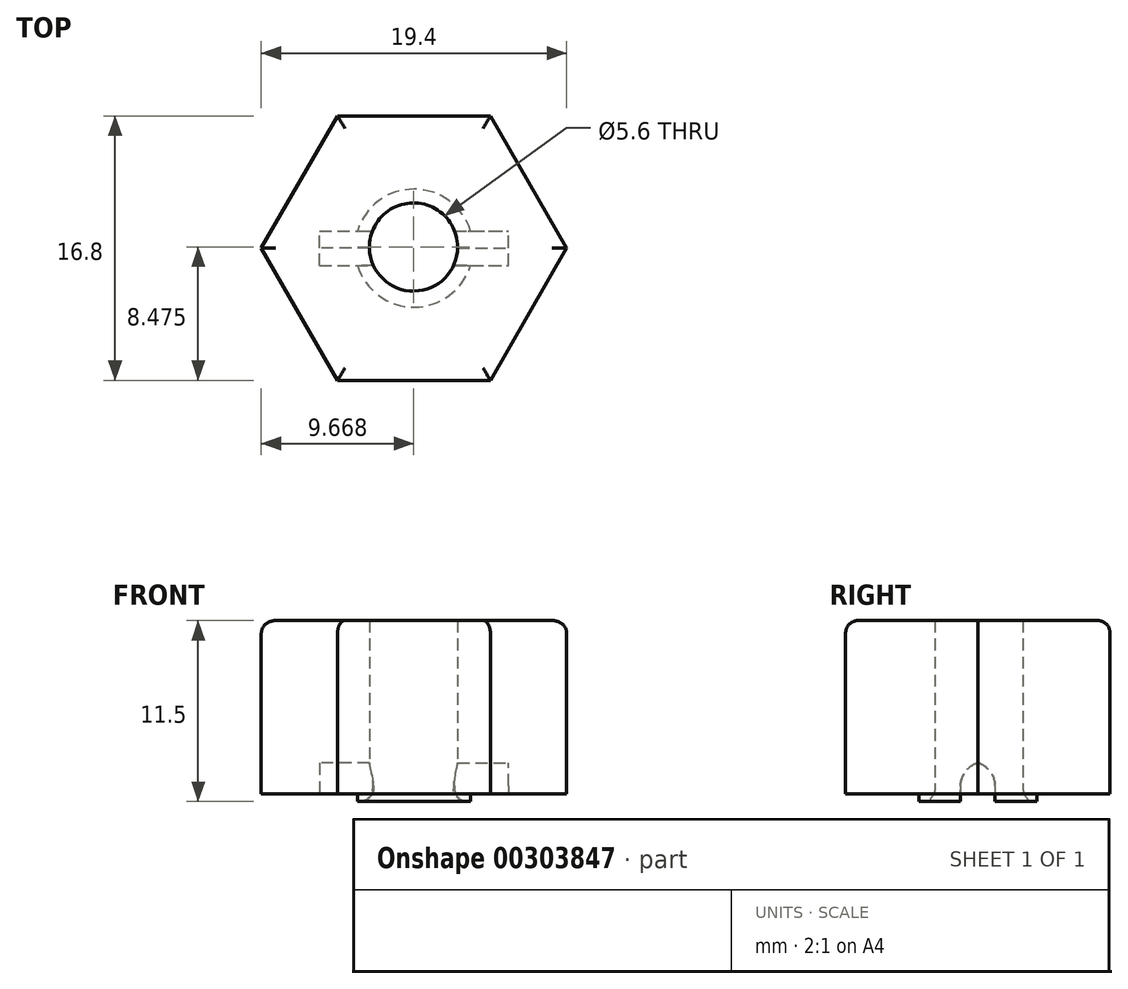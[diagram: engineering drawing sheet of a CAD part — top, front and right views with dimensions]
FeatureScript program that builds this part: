
annotation { "Feature Type Name" : "Feature", "Feature Type Description" : "" }
export const myFeature = defineFeature(function(context is Context, id is Id, definition is map)
    precondition{}
    {
        {
            var Q0;
            Q0=qCreatedBy(makeId("Top.planeOp"),FACE);
            var sketch = newSketch(context, id + "F0", { "sketchPlane" : qUnion([Q0])});
            skCircle(sketch, "E0.cCircle", {"center": v(0, 0) * mm, "radius": 8.4 * mm, "construction": true});
            skLineSegment(sketch, "E0.0", {"start": v(9.7, 0) * mm, "end": v(4.85, -8.4) * mm});
            skLineSegment(sketch, "E0.1", {"start": v(4.85, -8.4) * mm, "end": v(-4.85, -8.4) * mm});
            skLineSegment(sketch, "E0.2", {"start": v(-4.85, -8.4) * mm, "end": v(-9.7, 0) * mm});
            skLineSegment(sketch, "E0.3", {"start": v(-9.7, 0) * mm, "end": v(-4.85, 8.4) * mm});
            skLineSegment(sketch, "E0.4", {"start": v(-4.85, 8.4) * mm, "end": v(4.85, 8.4) * mm});
            skLineSegment(sketch, "E0.5", {"start": v(4.85, 8.4) * mm, "end": v(9.7, 0) * mm});
            skPoint(sketch, "E0.0.midPoint", {"position": v(7.27, -4.2) * mm});
            skCircle(sketch, "E1", {"center": v(-0.03, 0.07) * mm, "radius": 2.8 * mm});
            skSolve(sketch);
        }
        {
            var Q0;
            Q0=makeQuery(id+"F0.imprint","IMPRINT",FACE,{"disambiguationData":[TD([[makeQuery(id+"F0.imprint","IMPRINT",EDGE,{"derivedFrom":sQuery(id+"F0.wireOp",EDGE,"E0.0")}),-1.0]])]});
            extrude(context, id + "F1", {"entities" : qUnion([Q0]), "depth" : 11 * mm, "offsetDistance" : 25 * mm});
        }
        {
            var Q0;
            Q0=qCreatedBy(makeId("Top.planeOp"),FACE);
            var sketch = newSketch(context, id + "F2", { "sketchPlane" : qUnion([Q0])});
            skLineSegment(sketch, "E2.bottom", {"start": v(-6, -1.1) * mm, "end": v(6, -1.1) * mm});
            skLineSegment(sketch, "E2.top", {"start": v(-6, 1.1) * mm, "end": v(6, 1.1) * mm});
            skLineSegment(sketch, "E2.left", {"start": v(-6, -1.1) * mm, "end": v(-6, 1.1) * mm});
            skLineSegment(sketch, "E2.right", {"start": v(6, -1.1) * mm, "end": v(6, 1.1) * mm});
            skCircle(sketch, "E3", {"center": v(0, 0) * mm, "radius": 3.75 * mm});
            skSolve(sketch);
        }
        {
            var Q0;
            Q0=makeQuery(id+"F2.imprint","IMPRINT",FACE,{"disambiguationData":[TD([[makeQuery(id+"F2.imprint","IMPRINT",EDGE,{"derivedFrom":sQuery(id+"F2.wireOp",EDGE,"E2.bottom")}),1.0]])]});
            extrude(context, id + "F3", {"entities" : qUnion([Q0]), "operationType" : NewBodyOperationType.REMOVE, "depth" : 2 * mm, "offsetDistance" : 25 * mm});
        }
        {
            var Q0;
            Q0=makeQuery(id+"F1.opExtrude","CAP_FACE",FACE,{"disambiguationData":[OSD([sQuery(id+"F0.wireOp",EDGE,"E0.0"),sQuery(id+"F0.wireOp",EDGE,"E0.1"),sQuery(id+"F0.wireOp",EDGE,"E0.2"),sQuery(id+"F0.wireOp",EDGE,"E0.3"),sQuery(id+"F0.wireOp",EDGE,"E0.4"),sQuery(id+"F0.wireOp",EDGE,"E0.5"),sQuery(id+"F0.wireOp",EDGE,"E1")])],"isStart":true});
            var sketch = newSketch(context, id + "F4", { "sketchPlane" : qUnion([Q0])});
            skCircle(sketch, "E4", {"center": v(0, 0) * mm, "radius": 3.75 * mm});
            skSolve(sketch);
        }
        {
            var Q0;
            {var subQ1=sQuery(id+"F0.wireOp",EDGE,"E1");var subQ4=sQuery(id+"F2.wireOp",EDGE,"E2.bottom");var subQ5=makeQuery(id+"F3.opExtrude","SWEPT_FACE",FACE,{"disambiguationData":[OSD([subQ4])]});var subQ11=makeQuery(id+"F3.boolean.opBoolean","SPLIT",EDGE,{"disambiguationData":[TD([subQ5])],"derivedFrom":makeQuery(id+"F1.opExtrude","CAP_EDGE",EDGE,{"disambiguationData":[OSD([subQ1])],"isStart":true})});Q0=makeQuery(id+"F4.imprint","IMPRINT",FACE,{"disambiguationData":[TD([[makeQuery(id+"F4.imprint","IMPRINT",EDGE,{"derivedFrom":subQ11}),1.0]])]});}
            extrude(context, id + "F5", {"entities" : qUnion([Q0]), "operationType" : NewBodyOperationType.ADD, "depth" : 0.5 * mm});
        }
        {
            var Q0;
            {var subQ1=sQuery(id+"F0.wireOp",EDGE,"E1");var subQ3=sQuery(id+"F2.wireOp",EDGE,"E2.top");var subQ4=makeQuery(id+"F3.opExtrude","SWEPT_FACE",FACE,{"disambiguationData":[OSD([subQ3])]});var subQ11=makeQuery(id+"F3.boolean.opBoolean","SPLIT",EDGE,{"disambiguationData":[TD([subQ4])],"derivedFrom":makeQuery(id+"F1.opExtrude","CAP_EDGE",EDGE,{"disambiguationData":[OSD([subQ1])],"isStart":true})});Q0=makeQuery(id+"F4.imprint","IMPRINT",FACE,{"disambiguationData":[TD([[makeQuery(id+"F4.imprint","IMPRINT",EDGE,{"derivedFrom":subQ11}),1.0]])]});}
            extrude(context, id + "F6", {"entities" : qUnion([Q0]), "operationType" : NewBodyOperationType.ADD, "depth" : 0.5 * mm});
        }
        {
            var Q0;
            Q0=makeQuery(id+"F6.opExtrude","CAP_EDGE",EDGE,{"disambiguationData":[OSD([sQuery(id+"F0.wireOp",EDGE,"E1")])],"isStart":false});
            var Q1;
            Q1=makeQuery(id+"F5.opExtrude","CAP_EDGE",EDGE,{"disambiguationData":[OSD([sQuery(id+"F0.wireOp",EDGE,"E1")])],"isStart":false});
            fillet(context, id + "F7", {"entities" : qUnion([Q0, Q1]), "radius" : 0.8 * mm, "tangentPropagation" : true, "allowEdgeOverflow" : false});
        }
        {
            var Q0;
            {var subQ0=sQuery(id+"F2.wireOp",EDGE,"E2.right");var subQ1=sQuery(id+"F2.wireOp",EDGE,"E2.top");Q0=makeQuery(id+"F3.boolean.opBoolean","COPY",EDGE,{"disambiguationData":[TD([makeQuery(id+"F3.opExtrude","SWEPT_FACE",FACE,{"disambiguationData":[OSD([subQ0])]})])],"derivedFrom":makeQuery(id+"F3.opExtrude","CAP_EDGE",EDGE,{"disambiguationData":[OSD([subQ1])],"isStart":false})});}
            var Q1;
            {var subQ0=sQuery(id+"F2.wireOp",EDGE,"E2.bottom");var subQ1=sQuery(id+"F2.wireOp",EDGE,"E2.right");Q1=makeQuery(id+"F3.boolean.opBoolean","COPY",EDGE,{"disambiguationData":[TD([makeQuery(id+"F3.opExtrude","SWEPT_FACE",FACE,{"disambiguationData":[OSD([subQ1])]})])],"derivedFrom":makeQuery(id+"F3.opExtrude","CAP_EDGE",EDGE,{"disambiguationData":[OSD([subQ0])],"isStart":false})});}
            var Q2;
            {var subQ0=sQuery(id+"F2.wireOp",EDGE,"E2.bottom");var subQ1=sQuery(id+"F2.wireOp",EDGE,"E2.left");Q2=makeQuery(id+"F3.boolean.opBoolean","COPY",EDGE,{"disambiguationData":[TD([makeQuery(id+"F3.opExtrude","SWEPT_FACE",FACE,{"disambiguationData":[OSD([subQ1])]})])],"derivedFrom":makeQuery(id+"F3.opExtrude","CAP_EDGE",EDGE,{"disambiguationData":[OSD([subQ0])],"isStart":false})});}
            var Q3;
            {var subQ0=sQuery(id+"F2.wireOp",EDGE,"E2.left");var subQ1=sQuery(id+"F2.wireOp",EDGE,"E2.top");Q3=makeQuery(id+"F3.boolean.opBoolean","COPY",EDGE,{"disambiguationData":[TD([makeQuery(id+"F3.opExtrude","SWEPT_FACE",FACE,{"disambiguationData":[OSD([subQ0])]})])],"derivedFrom":makeQuery(id+"F3.opExtrude","CAP_EDGE",EDGE,{"disambiguationData":[OSD([subQ1])],"isStart":false})});}
            fillet(context, id + "F8", {"entities" : qUnion([Q0, Q1, Q2, Q3]), "radius" : 1.5 * mm, "tangentPropagation" : true, "allowEdgeOverflow" : false});
        }
        {
            var Q0;
            Q0=makeQuery(id+"F1.opExtrude","CAP_EDGE",EDGE,{"disambiguationData":[OSD([sQuery(id+"F0.wireOp",EDGE,"E0.1")])],"isStart":false});
            var Q1;
            Q1=makeQuery(id+"F1.opExtrude","CAP_EDGE",EDGE,{"disambiguationData":[OSD([sQuery(id+"F0.wireOp",EDGE,"E0.0")])],"isStart":false});
            var Q2;
            Q2=makeQuery(id+"F1.opExtrude","CAP_EDGE",EDGE,{"disambiguationData":[OSD([sQuery(id+"F0.wireOp",EDGE,"E0.5")])],"isStart":false});
            var Q3;
            Q3=makeQuery(id+"F1.opExtrude","CAP_EDGE",EDGE,{"disambiguationData":[OSD([sQuery(id+"F0.wireOp",EDGE,"E0.4")])],"isStart":false});
            var Q4;
            Q4=makeQuery(id+"F1.opExtrude","CAP_EDGE",EDGE,{"disambiguationData":[OSD([sQuery(id+"F0.wireOp",EDGE,"E0.3")])],"isStart":false});
            var Q5;
            Q5=makeQuery(id+"F1.opExtrude","CAP_EDGE",EDGE,{"disambiguationData":[OSD([sQuery(id+"F0.wireOp",EDGE,"E0.2")])],"isStart":false});
            fillet(context, id + "F9", {"entities" : qUnion([Q0, Q1, Q2, Q3, Q4, Q5]), "radius" : 0.8 * mm, "tangentPropagation" : true, "allowEdgeOverflow" : false});
        }
    });
